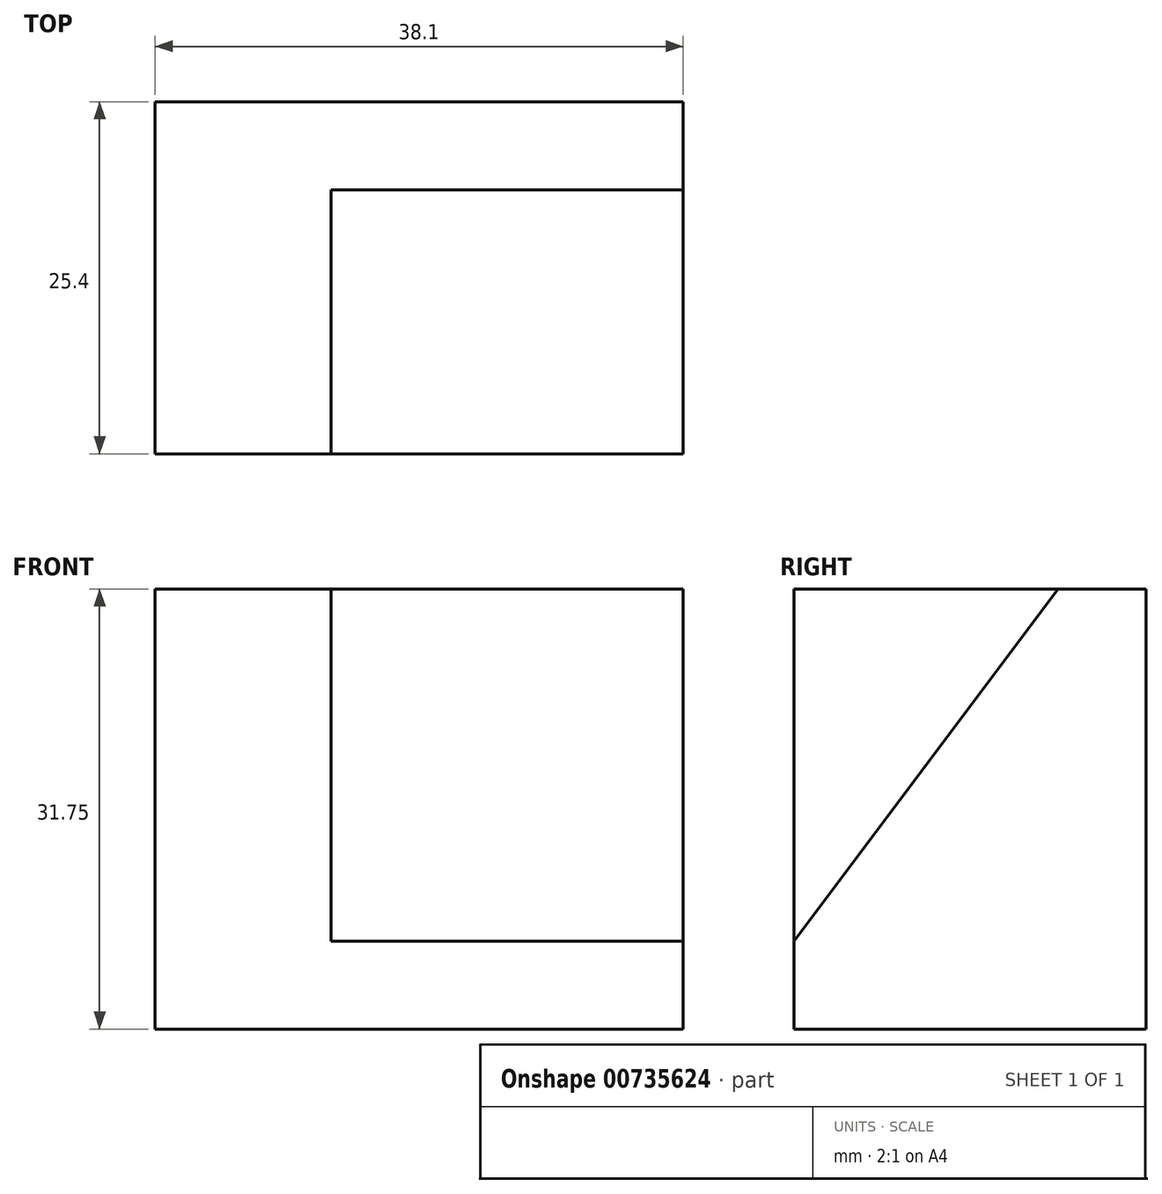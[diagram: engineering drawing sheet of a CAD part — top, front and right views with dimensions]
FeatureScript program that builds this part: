
annotation { "Feature Type Name" : "Feature", "Feature Type Description" : "" }
export const myFeature = defineFeature(function(context is Context, id is Id, definition is map)
    precondition{}
    {
        {
            var Q0;
            Q0=qCreatedBy(makeId("Front.planeOp"),FACE);
            var sketch = newSketch(context, id + "F0", { "sketchPlane" : qUnion([Q0])});
            skLineSegment(sketch, "E0.bottom", {"start": v(0, 0) * mm, "end": v(38.1, 0) * mm});
            skLineSegment(sketch, "E0.top", {"start": v(0, 31.75) * mm, "end": v(38.1, 31.75) * mm});
            skLineSegment(sketch, "E0.left", {"start": v(0, 0) * mm, "end": v(0, 31.75) * mm});
            skLineSegment(sketch, "E0.right", {"start": v(38.1, 0) * mm, "end": v(38.1, 31.75) * mm});
            skSolve(sketch);
        }
        {
            var Q0;
            Q0=makeQuery(id+"F0.imprint","IMPRINT",FACE,{"disambiguationData":[TD([[makeQuery(id+"F0.imprint","IMPRINT",EDGE,{"derivedFrom":sQuery(id+"F0.wireOp",EDGE,"E0.bottom")}),1.0]])]});
            extrude(context, id + "F1", {"entities" : qUnion([Q0]), "depth" : 25.4 * mm, "offsetDistance" : 25.4 * mm});
        }
        {
            var Q0;
            Q0=makeQuery(id+"F1.opExtrude","SWEPT_FACE",FACE,{"disambiguationData":[OSD([sQuery(id+"F0.wireOp",EDGE,"E0.right")])]});
            var sketch = newSketch(context, id + "F2", { "sketchPlane" : qUnion([Q0])});
            skLineSegment(sketch, "E1", {"start": v(-6.35, 31.75) * mm, "end": v(-25.4, 6.35) * mm});
            skLineSegment(sketch, "E2", {"start": v(-25.4, 6.35) * mm, "end": v(-25.4, 31.75) * mm});
            skLineSegment(sketch, "E3", {"start": v(-25.4, 31.75) * mm, "end": v(-6.35, 31.75) * mm});
            skSolve(sketch);
        }
        {
            var Q0;
            Q0=makeQuery(id+"F2.imprint","IMPRINT",FACE,{"disambiguationData":[TD([[makeQuery(id+"F2.imprint","IMPRINT",EDGE,{"derivedFrom":sQuery(id+"F2.wireOp",EDGE,"E1")}),-1.0]])]});
            extrude(context, id + "F3", {"entities" : qUnion([Q0]), "operationType" : NewBodyOperationType.REMOVE, "oppositeDirection" : true, "depth" : 25.4 * mm, "offsetDistance" : 25.4 * mm});
        }
    });
